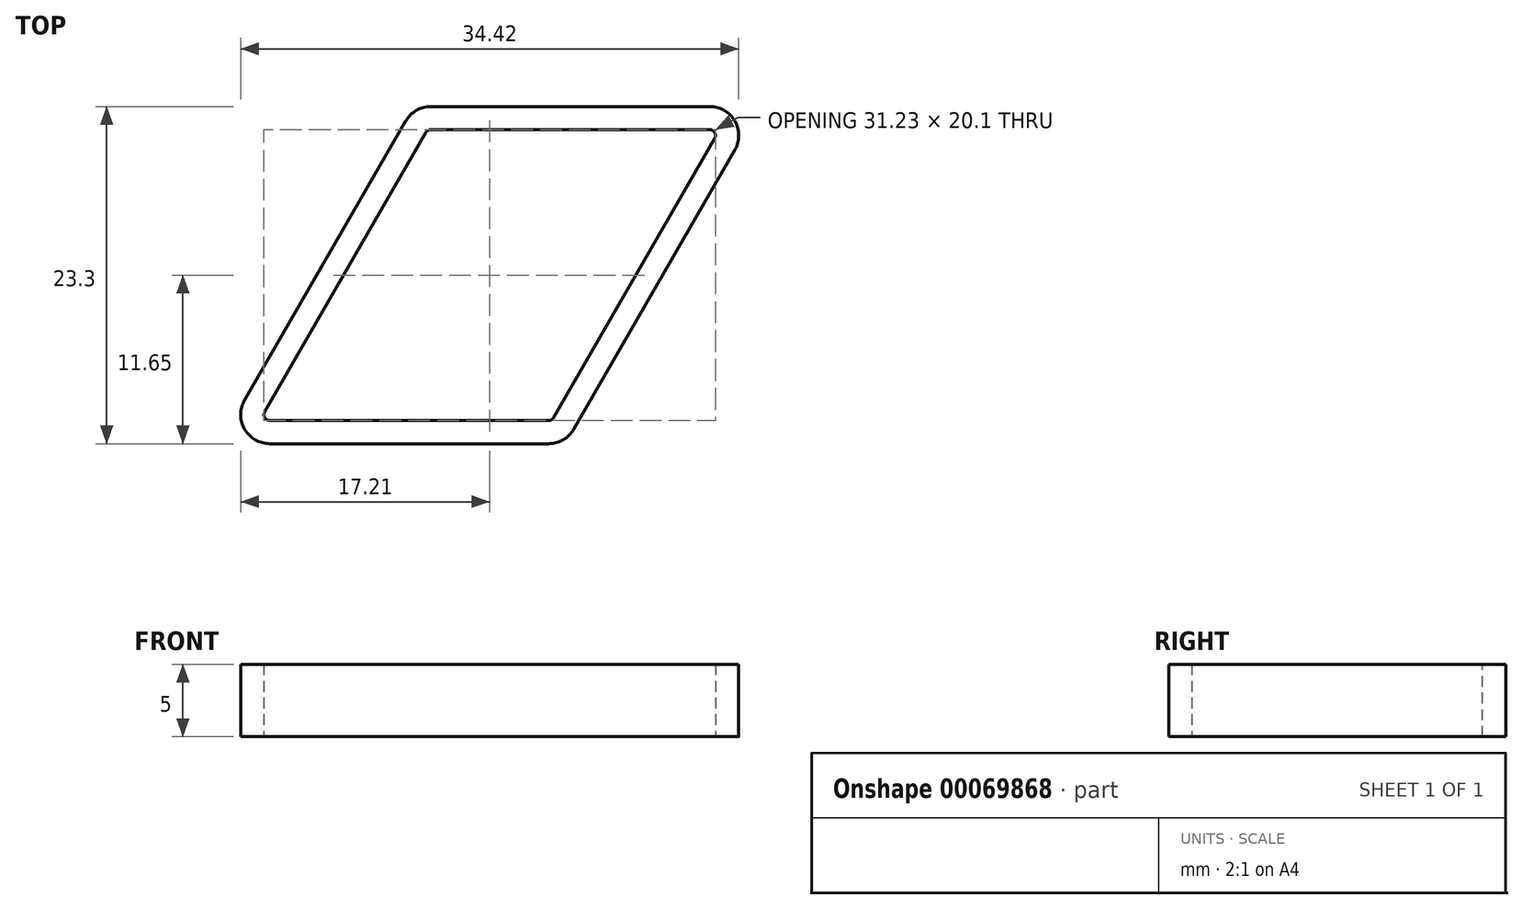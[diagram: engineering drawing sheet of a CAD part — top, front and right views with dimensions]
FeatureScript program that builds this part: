
annotation { "Feature Type Name" : "Feature", "Feature Type Description" : "" }
export const myFeature = defineFeature(function(context is Context, id is Id, definition is map)
    precondition{}
    {
        {
            var Q0;
            Q0=qCreatedBy(makeId("Top.planeOp"),FACE);
            var sketch = newSketch(context, id + "F0", { "sketchPlane" : qUnion([Q0])});
            skLineSegment(sketch, "E0", {"start": v(0, 0) * mm, "end": v(11.03, 19.1) * mm});
            skLineSegment(sketch, "E1", {"start": v(11.03, 19.1) * mm, "end": v(30.08, 19.1) * mm});
            skLineSegment(sketch, "E2", {"start": v(30.08, 19.1) * mm, "end": v(19.05, 0) * mm});
            skLineSegment(sketch, "E3", {"start": v(19.05, 0) * mm, "end": v(0, 0) * mm});
            skLineSegment(sketch, "E4.0", {"start": v(-3.64, -2.1) * mm, "end": v(9.81, 21.2) * mm});
            skLineSegment(sketch, "E4.1", {"start": v(20.26, -2.1) * mm, "end": v(-3.64, -2.1) * mm});
            skLineSegment(sketch, "E4.2", {"start": v(33.72, 21.2) * mm, "end": v(20.26, -2.1) * mm});
            skLineSegment(sketch, "E4.3", {"start": v(9.81, 21.2) * mm, "end": v(33.72, 21.2) * mm});
            skPoint(sketch, "E5", {"position": v(9.53, 0) * mm});
            skSolve(sketch);
        }
        {
            var Q0;
            Q0=makeQuery(id+"F0.imprint","IMPRINT",FACE,{"disambiguationData":[TD([[makeQuery(id+"F0.imprint","IMPRINT",EDGE,{"derivedFrom":sQuery(id+"F0.wireOp",EDGE,"E0")}),1.0]])]});
            var Q1;
            Q1=makeQuery(id+"F0.imprint","IMPRINT",FACE,{"disambiguationData":[TD([[makeQuery(id+"F0.imprint","IMPRINT",EDGE,{"derivedFrom":sQuery(id+"F0.wireOp",EDGE,"E0")}),-1.0]])]});
            extrude(context, id + "F1", {"entities" : qUnion([Q0, Q1]), "depth" : 5 * mm});
        }
        {
            var Q0;
            Q0=makeQuery(id+"F1.opExtrude","SWEPT_EDGE",EDGE,{"disambiguationData":[OSD([sQuery(id+"F0.wireOp",EDGE,"E4.0"),sQuery(id+"F0.wireOp",EDGE,"E4.1")])]});
            var Q1;
            Q1=makeQuery(id+"F1.opExtrude","SWEPT_EDGE",EDGE,{"disambiguationData":[OSD([sQuery(id+"F0.wireOp",EDGE,"E4.1"),sQuery(id+"F0.wireOp",EDGE,"E4.2")])]});
            var Q2;
            Q2=makeQuery(id+"F1.opExtrude","SWEPT_EDGE",EDGE,{"disambiguationData":[OSD([sQuery(id+"F0.wireOp",EDGE,"E4.2"),sQuery(id+"F0.wireOp",EDGE,"E4.3")])]});
            var Q3;
            Q3=makeQuery(id+"F1.opExtrude","SWEPT_EDGE",EDGE,{"disambiguationData":[OSD([sQuery(id+"F0.wireOp",EDGE,"E4.0"),sQuery(id+"F0.wireOp",EDGE,"E4.3")])]});
            fillet(context, id + "F2", {"entities" : qUnion([Q0, Q1, Q2, Q3]), "radius" : 2 * mm, "tangentPropagation" : true, "allowEdgeOverflow" : false});
        }
        {
            var Q0;
            Q0=makeQuery(id+"F1.opExtrude","CAP_FACE",FACE,{"disambiguationData":[OSD([sQuery(id+"F0.wireOp",EDGE,"E4.0"),sQuery(id+"F0.wireOp",EDGE,"E4.1"),sQuery(id+"F0.wireOp",EDGE,"E4.2"),sQuery(id+"F0.wireOp",EDGE,"E4.3")])],"isStart":false});
            var Q1;
            Q1=makeQuery(id+"F1.opExtrude","CAP_FACE",FACE,{"disambiguationData":[OSD([sQuery(id+"F0.wireOp",EDGE,"E4.0"),sQuery(id+"F0.wireOp",EDGE,"E4.1"),sQuery(id+"F0.wireOp",EDGE,"E4.2"),sQuery(id+"F0.wireOp",EDGE,"E4.3")])],"isStart":true});
            shell(context, id + "F3", {"entities" : qUnion([Q0, Q1]), "thickness" : 1.6 * mm});
        }
    });
